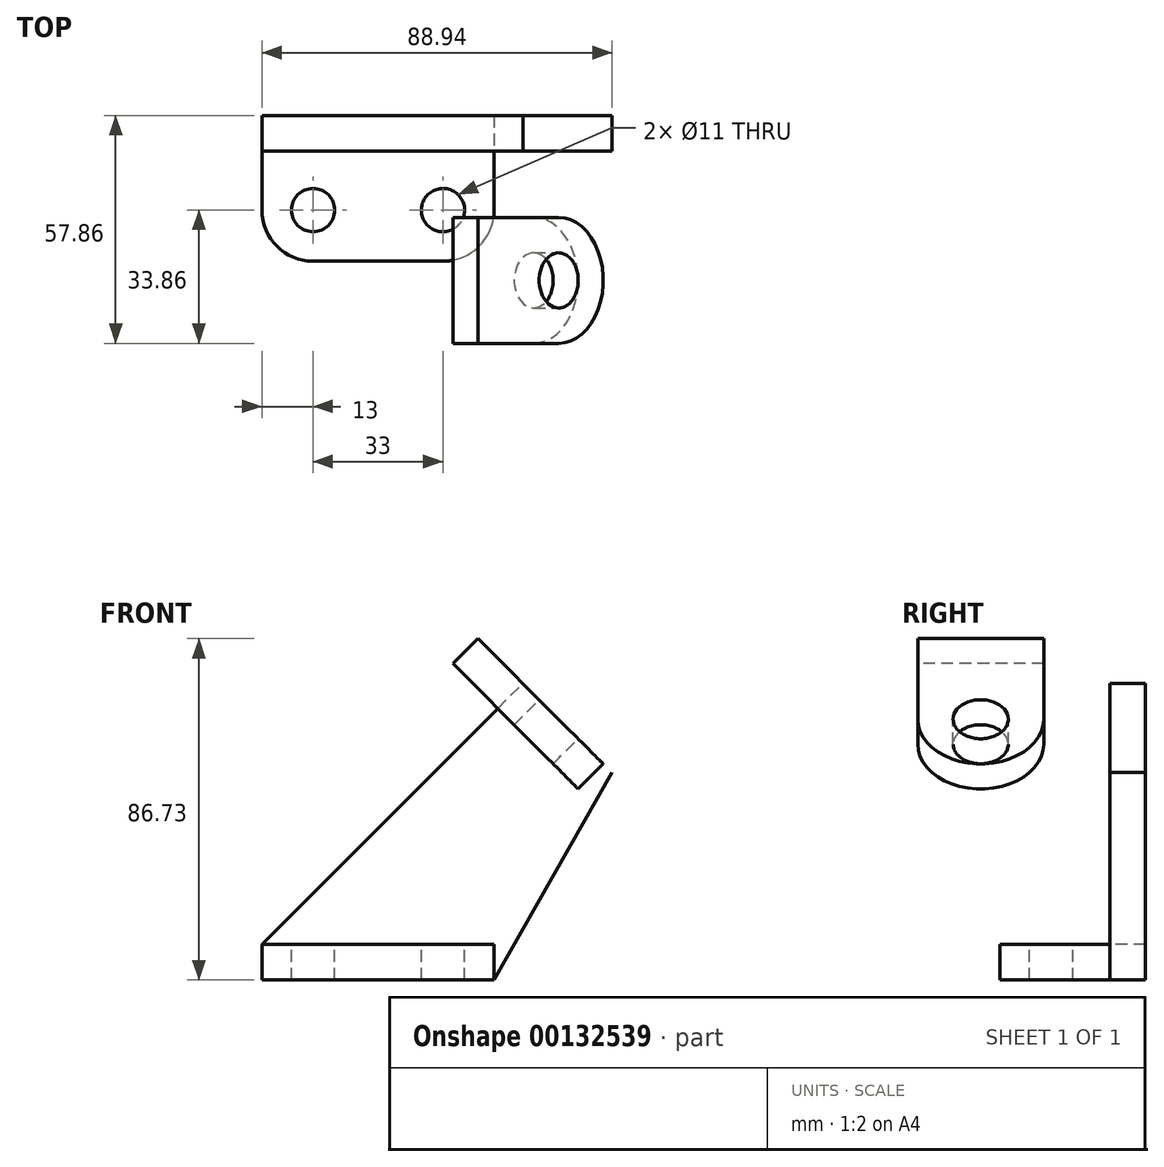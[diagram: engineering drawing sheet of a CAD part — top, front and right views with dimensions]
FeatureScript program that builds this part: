
annotation { "Feature Type Name" : "Feature", "Feature Type Description" : "" }
export const myFeature = defineFeature(function(context is Context, id is Id, definition is map)
    precondition{}
    {
        {
            var Q0;
            Q0=qCreatedBy(makeId("Top.planeOp"),FACE);
            var sketch = newSketch(context, id + "F0", { "sketchPlane" : qUnion([Q0])});
            skLineSegment(sketch, "E0", {"start": v(-16.5, 0) * mm, "end": v(16.5, 0) * mm});
            skLineSegment(sketch, "E1", {"start": v(29.5, 37) * mm, "end": v(-29.5, 37) * mm});
            skCircle(sketch, "E2", {"center": v(16.5, 13) * mm, "radius": 5.5 * mm});
            skCircle(sketch, "E3", {"center": v(-16.5, 13) * mm, "radius": 5.5 * mm});
            skLineSegment(sketch, "E4", {"start": v(-29.5, 37) * mm, "end": v(-29.5, 13) * mm});
            skArc(sketch, "E5", {"start": v(-29.5, 13) * mm, "mid": v(-25.7, 3.8) * mm, "end": v(-16.5, 0) * mm});
            skLineSegment(sketch, "E6", {"start": v(29.5, 37) * mm, "end": v(29.5, 13) * mm});
            skArc(sketch, "E7", {"start": v(16.5, 0) * mm, "mid": v(25.7, 3.8) * mm, "end": v(29.5, 13) * mm});
            skSolve(sketch);
        }
        {
            var Q0;
            Q0 = qSketchRegion(id + "F0", true);
            extrude(context, id + "F1", {"entities" : qUnion([Q0]), "oppositeDirection" : true, "depth" : 9 * mm});
        }
        {
            var Q0;
            Q0 = qSketchRegion(id + "F0", true);
            extrude(context, id + "F2", {"entities" : qUnion([Q0]), "oppositeDirection" : true, "depth" : 9 * mm});
        }
        {
            var Q0;
            Q0=makeQuery(id+"F1.opExtrude","SWEPT_FACE",FACE,{"disambiguationData":[OSD([sQuery(id+"F0.wireOp",EDGE,"E0")])]});
            var sketch = newSketch(context, id + "F3", { "sketchPlane" : qUnion([Q0])});
            skLineSegment(sketch, "E8", {"start": v(-0.47, 55) * mm, "end": v(96.73, 55) * mm});
            skLineSegment(sketch, "E9", {"start": v(-0.47, 55) * mm, "end": v(-0.47, 55) * mm});
            skLineSegment(sketch, "E10", {"start": v(29.5, 0) * mm, "end": v(-29.5, 0) * mm});
            skPoint(sketch, "E11", {"position": v(48.13, 55) * mm});
            skLineSegment(sketch, "E12", {"start": v(36.81, 66.31) * mm, "end": v(59.44, 43.69) * mm});
            skLineSegment(sketch, "E13", {"start": v(-0.47, 55) * mm, "end": v(96.73, 55) * mm, "construction": true});
            skLineSegment(sketch, "E14", {"start": v(59.44, 43.69) * mm, "end": v(29.5, -9) * mm});
            skLineSegment(sketch, "E15", {"start": v(29.5, -9) * mm, "end": v(29.5, 0) * mm});
            skLineSegment(sketch, "E16", {"start": v(-29.5, 0) * mm, "end": v(36.81, 66.31) * mm});
            skSolve(sketch);
        }
        {
            var Q0;
            Q0 = qSketchRegion(id + "F3", true);
            var Q1;
            Q1=makeQuery(id+"F1.opExtrude","SWEPT_FACE",FACE,{"disambiguationData":[OSD([sQuery(id+"F0.wireOp",EDGE,"E1")])]});
            extrude(context, id + "F4", {"entities" : qUnion([Q0]), "operationType" : NewBodyOperationType.ADD, "endBound" : BoundingType.UP_TO_SURFACE, "oppositeDirection" : true, "endBoundEntityFace" : qUnion([Q1]), "depth" : 25 * mm});
        }
        {
            var Q0;
            Q0 = qSketchRegion(id + "F3", true);
            extrude(context, id + "F5", {"entities" : qUnion([Q0]), "operationType" : NewBodyOperationType.REMOVE, "oppositeDirection" : true, "depth" : 28 * mm});
        }
        {
            var Q0;
            Q0=makeQuery(id+"F4.opExtrude","SWEPT_FACE",FACE,{"disambiguationData":[OSD([sQuery(id+"F3.wireOp",EDGE,"E12")])]});
            var sketch = newSketch(context, id + "F6", { "sketchPlane" : qUnion([Q0])});
            skLineSegment(sketch, "E17", {"start": v(-20.86, 37) * mm, "end": v(-20.86, 8) * mm});
            skPoint(sketch, "E17.endSnap0", {"position": v(-20.86, 32.5) * mm});
            skLineSegment(sketch, "E18", {"start": v(11.14, 37) * mm, "end": v(11.14, 8) * mm});
            skArc(sketch, "E19", {"start": v(-20.86, 8) * mm, "mid": v(-4.86, -8) * mm, "end": v(11.14, 8) * mm});
            skCircle(sketch, "E20", {"center": v(-4.86, 8) * mm, "radius": 7 * mm});
            skLineSegment(sketch, "E21", {"start": v(11.14, 37) * mm, "end": v(-20.86, 37) * mm});
            skSolve(sketch);
        }
        {
            var Q0;
            Q0 = qSketchRegion(id + "F6", true);
            extrude(context, id + "F7", {"entities" : qUnion([Q0]), "operationType" : NewBodyOperationType.ADD, "oppositeDirection" : true, "depth" : 9 * mm});
        }
    });
